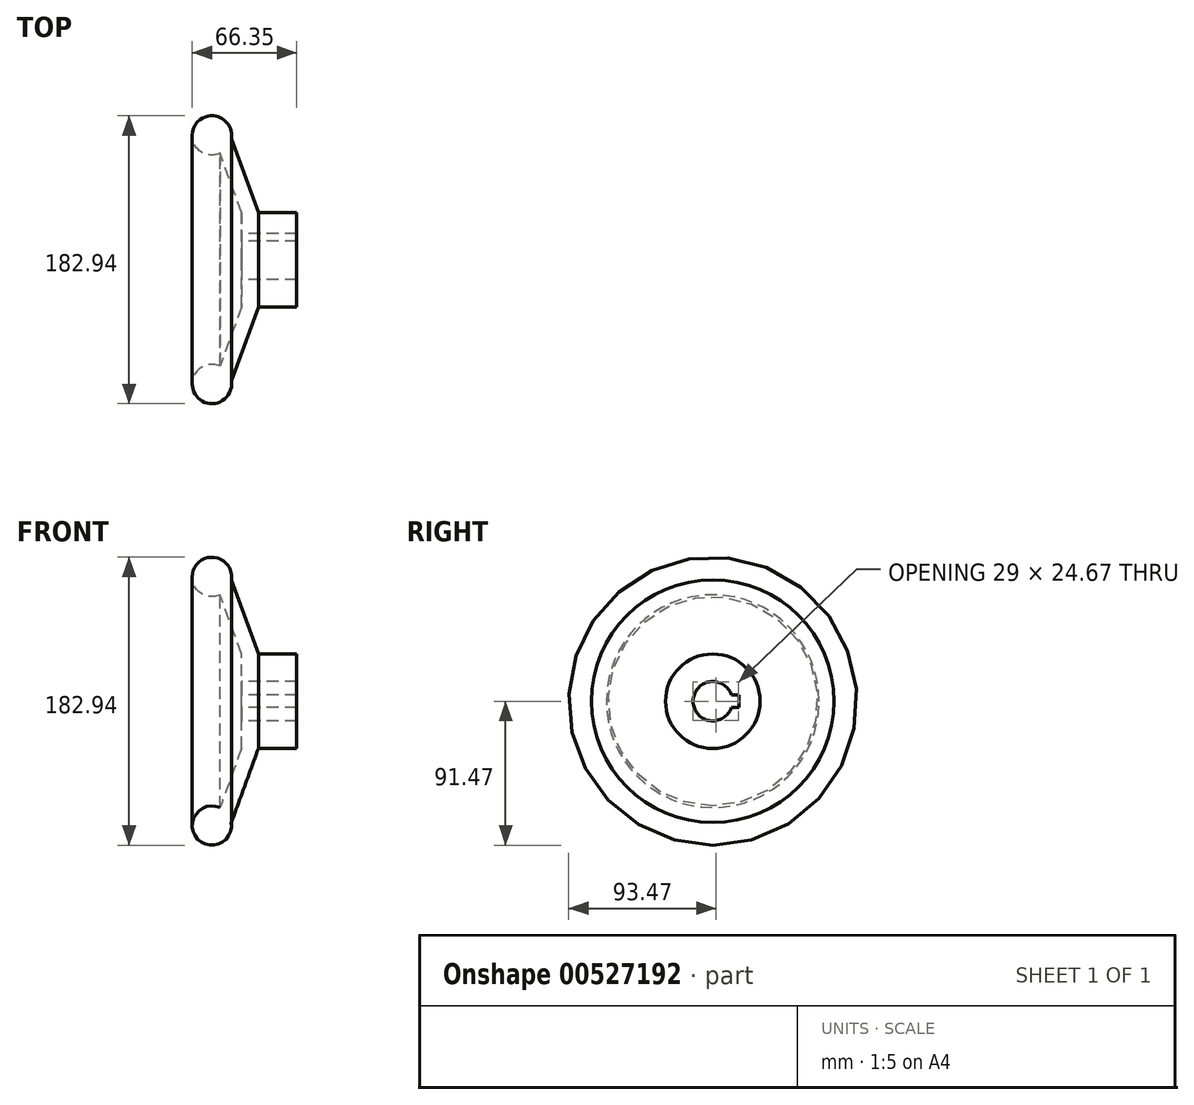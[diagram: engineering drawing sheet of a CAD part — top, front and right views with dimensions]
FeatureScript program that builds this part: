
annotation { "Feature Type Name" : "Feature", "Feature Type Description" : "" }
export const myFeature = defineFeature(function(context is Context, id is Id, definition is map)
    precondition{}
    {
        {
            var Q0;
            Q0=qCreatedBy(makeId("Front.planeOp"),FACE);
            var sketch = newSketch(context, id + "F0", { "sketchPlane" : qUnion([Q0])});
            skLineSegment(sketch, "E0.bottom", {"start": v(-8.2, 30) * mm, "end": v(16.16, 30) * mm});
            skLineSegment(sketch, "E0.top", {"start": v(-18.84, 0) * mm, "end": v(16.16, 0) * mm});
            skLineSegment(sketch, "E0.left", {"start": v(-18.84, 30) * mm, "end": v(-18.84, 0) * mm});
            skLineSegment(sketch, "E0.right", {"start": v(16.16, 30) * mm, "end": v(16.16, 0) * mm});
            skLineSegment(sketch, "E1", {"start": v(-18.84, 30) * mm, "end": v(-32.52, 67.58) * mm});
            skArc(sketch, "E2", {"start": v(-25.33, 77.07) * mm, "mid": v(-47.65, 86.52) * mm, "end": v(-32.52, 67.58) * mm});
            skLineSegment(sketch, "E3.0", {"start": v(-8.2, 30) * mm, "end": v(-25.33, 77.07) * mm});
            skLineSegment(sketch, "E4", {"start": v(0, 0) * mm, "end": v(-126.42, 0) * mm, "construction": true});
            skCircle(sketch, "E5", {"center": v(0, 0) * mm, "radius": 75 * mm, "construction": true});
            skLineSegment(sketch, "E6", {"start": v(-50.19, 0) * mm, "end": v(-50.19, 91.73) * mm, "construction": true});
            skSolve(sketch);
        }
        {
            var Q0;
            Q0=makeQuery(id+"F0.imprint","IMPRINT",FACE,{"disambiguationData":[TD([[makeQuery(id+"F0.imprint","IMPRINT",EDGE,{"derivedFrom":sQuery(id+"F0.wireOp",EDGE,"E0.bottom")}),-1.0]])]});
            var Q1;
            Q1=sQuery(id+"F0.wireOp",EDGE,"E4");
            revolve(context, id + "F1", {"entities" : qUnion([Q0]), "axis" : qUnion([Q1]), "revolveType" : RevolveType.FULL});
        }
        {
            var Q0;
            Q0=makeQuery(id+"F1.opRevolve","SWEPT_FACE",FACE,{"disambiguationData":[OSD([sQuery(id+"F0.wireOp",EDGE,"E0.left")])]});
            var sketch = newSketch(context, id + "F2", { "sketchPlane" : qUnion([Q0])});
            skPoint(sketch, "E7", {"position": v(0, 0) * mm});
            skCircle(sketch, "E8", {"center": v(0, 0) * mm, "radius": 12.5 * mm, "construction": true});
            skLineSegment(sketch, "E9.bottom", {"start": v(-16.5, -4) * mm, "end": v(-8.5, -4) * mm});
            skLineSegment(sketch, "E9.top", {"start": v(-16.5, 4) * mm, "end": v(-8.5, 4) * mm});
            skLineSegment(sketch, "E9.left", {"start": v(-16.5, -4) * mm, "end": v(-16.5, 4) * mm});
            skLineSegment(sketch, "E9.right", {"start": v(-8.5, -4) * mm, "end": v(-8.5, 4) * mm});
            skLineSegment(sketch, "E10", {"start": v(0, 0) * mm, "end": v(-23.37, 0) * mm, "construction": true});
            skSolve(sketch);
        }
        {
            var Q0;
            Q0=sQuery(id+"F2.wireOp",VERTEX,"E7");
            var Q1;
            Q1=makeQuery(id+"F1.opRevolve","SWEPT_BODY",BODY,{"disambiguationData":[OSD([sQuery(id+"F0.wireOp",EDGE,"E0.bottom"),sQuery(id+"F0.wireOp",EDGE,"E0.top"),sQuery(id+"F0.wireOp",EDGE,"E0.left"),sQuery(id+"F0.wireOp",EDGE,"E0.right"),sQuery(id+"F0.wireOp",EDGE,"E1"),sQuery(id+"F0.wireOp",EDGE,"E2"),sQuery(id+"F0.wireOp",EDGE,"E3.0")])]});
            hole(context, id + "F3", {"style" : HoleStyle.SIMPLE, "endStyle" : HoleEndStyle.THROUGH, "holeDiameter" : 25 * mm, "isTappedThrough" : true, "tappedDepth" : 12 * mm, "tapClearance" : 3, "locations" : qUnion([Q0]), "scope" : qUnion([Q1])});
        }
        {
            var Q0;
            Q0=makeQuery(id+"F2.imprint","IMPRINT",FACE,{"disambiguationData":[TD([[makeQuery(id+"F2.imprint","IMPRINT",EDGE,{"derivedFrom":sQuery(id+"F2.wireOp",EDGE,"E9.bottom")}),1.0]])]});
            extrude(context, id + "F4", {"entities" : qUnion([Q0]), "operationType" : NewBodyOperationType.REMOVE, "oppositeDirection" : true, "depth" : 50 * mm, "offsetDistance" : 25 * mm});
        }
    });
